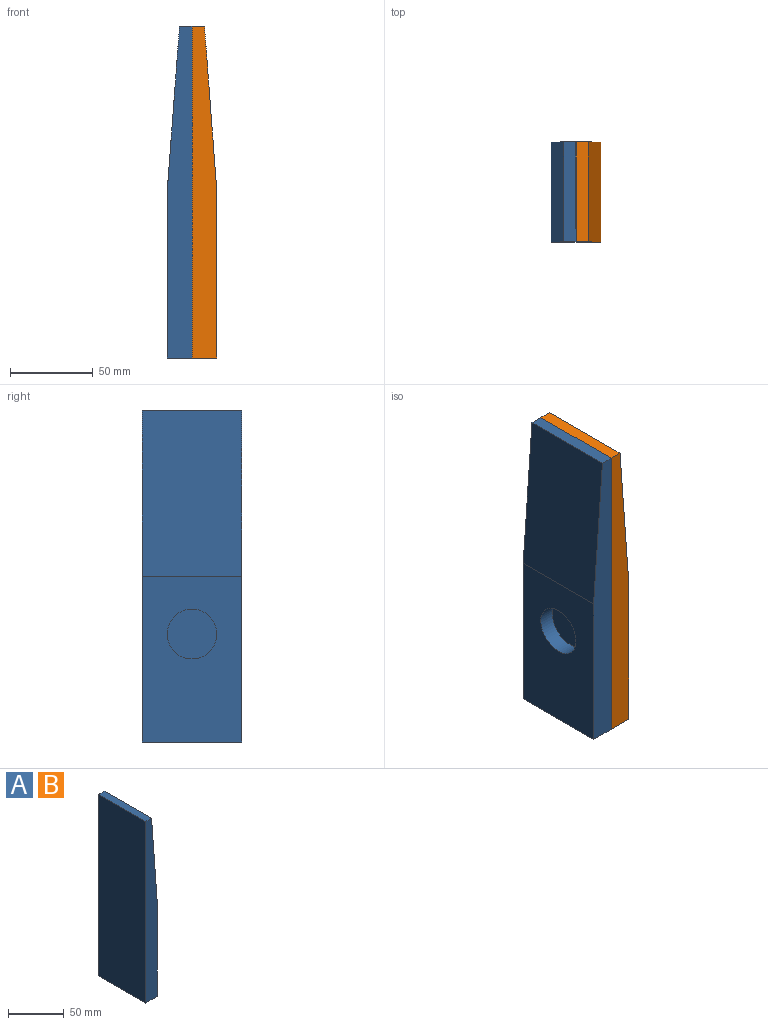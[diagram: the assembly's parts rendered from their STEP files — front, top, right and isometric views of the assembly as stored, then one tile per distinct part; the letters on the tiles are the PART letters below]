
ASSEMBLY  parts=2 mates=1
PART A: 9 faces, bbox 15x60x200 mm
  f0: plane 200x60mm, normal (-1,0,0), area 12000mm2, adj f1,f4,f5,f6
  f1: plane 60x15mm, normal (0,0,-1), area 900mm2, adj f0,f2,f5,f6
  f2: plane 100x60mm, normal (1,0,0), area 5293.1mm2, adj f1,f3,f5,f6,f7
  f3: plane 100x60mm, normal (1,0,0.07), area 6016.9mm2, adj f2,f4,f5,f6
  f4: plane 60x7.5mm, normal (0,0,1), area 450mm2, adj f0,f3,f5,f6
  f5: plane 200x15mm, normal (0,-1,0), area 2625mm2, adj f0,f1,f2,f3,f4
  f6: plane 200x15mm, normal (0,1,0), area 2625mm2, adj f0,f1,f2,f3,f4
  f7: cylinder r=15mm len=30mm, axis (1,0,0), area 942.5mm2, adj f2,f8
  f8: plane 30x30mm, normal (1,0,0), area 706.9mm2, adj f7
PART B: same geometry as A
PLACE A rot(axis=(0,0,-1),180deg) t=(-15.58,70.71,-22)mm
PLACE B rot(axis=(0,0,1),0deg) t=(-15.58,30.71,-22)mm
MATE fastened B.f0 <-> A.f0  axis (-1,0,0) through (-15.58,50.71,78)mm
